annotation { "Feature Type Name" : "Feature", "Feature Type Description" : "" }
export const myFeature = defineFeature(function(context is Context, id is Id, definition is map)
    precondition{}
    {
        {
            var Q0;
            Q0=qCreatedBy(makeId("Top.planeOp"),FACE);
            var sketch = newSketch(context, id + "F0", { "sketchPlane" : qUnion([Q0])});
            skLineSegment(sketch, "E0.bottom", {"start": v(-839.09, -403.11) * mm, "end": v(831.05, -403.11) * mm});
            skLineSegment(sketch, "E0.left", {"start": v(-839.09, -403.11) * mm, "end": v(-839.09, -466.48) * mm});
            skLineSegment(sketch, "E0.right", {"start": v(831.05, -403.11) * mm, "end": v(831.05, -466.48) * mm});
            skLineSegment(sketch, "E1.bottom", {"start": v(761.55, -403.11) * mm, "end": v(831.05, -403.11) * mm});
            skLineSegment(sketch, "E1.top", {"start": v(761.55, 445.24) * mm, "end": v(831.05, 445.24) * mm});
            skLineSegment(sketch, "E1.left", {"start": v(761.55, -403.11) * mm, "end": v(761.55, 445.24) * mm});
            skLineSegment(sketch, "E1.right", {"start": v(831.05, -403.11) * mm, "end": v(831.05, 445.24) * mm});
            skLineSegment(sketch, "E2.bottom", {"start": v(761.55, 445.24) * mm, "end": v(-792.07, 445.24) * mm});
            skLineSegment(sketch, "E2.top", {"start": v(761.55, 390.05) * mm, "end": v(-792.07, 390.05) * mm});
            skLineSegment(sketch, "E2.left", {"start": v(761.55, 445.24) * mm, "end": v(761.55, 390.05) * mm});
            skLineSegment(sketch, "E2.right", {"start": v(-792.07, 445.24) * mm, "end": v(-792.07, 390.05) * mm});
            skLineSegment(sketch, "E3", {"start": v(-839.09, -466.48) * mm, "end": v(831.05, -466.48) * mm});
            skLineSegment(sketch, "E4.bottom", {"start": v(-792.07, 445.24) * mm, "end": v(-839.09, 445.24) * mm});
            skLineSegment(sketch, "E4.top", {"start": v(-792.07, -403.11) * mm, "end": v(-839.09, -403.11) * mm});
            skLineSegment(sketch, "E4.left", {"start": v(-792.07, 445.24) * mm, "end": v(-792.07, -403.11) * mm});
            skLineSegment(sketch, "E4.right", {"start": v(-839.09, 445.24) * mm, "end": v(-839.09, -403.11) * mm});
            skSolve(sketch);
        }
        {
            var Q0;
            Q0=makeQuery(id+"F0.imprint","IMPRINT",FACE,{"disambiguationData":[TD([[makeQuery(id+"F0.imprint","IMPRINT",EDGE,{"derivedFrom":sQuery(id+"F0.wireOp",EDGE,"E2.right")}),-1.0]])]});
            var Q1;
            {var subQ0=sQuery(id+"F0.wireOp",EDGE,"E0.left");Q1=makeQuery(id+"F0.imprint","IMPRINT",FACE,{"disambiguationData":[TD([[makeQuery(id+"F0.imprint","IMPRINT",EDGE,{"derivedFrom":subQ0}),1.0]])]});}
            var Q2;
            {var subQ0=sQuery(id+"F0.wireOp",EDGE,"E2.bottom");Q2=makeQuery(id+"F0.imprint","IMPRINT",FACE,{"disambiguationData":[TD([[makeQuery(id+"F0.imprint","IMPRINT",EDGE,{"derivedFrom":subQ0}),1.0]])]});}
            var Q3;
            {var subQ1=sQuery(id+"F0.wireOp",EDGE,"E1.top");Q3=makeQuery(id+"F0.imprint","IMPRINT",FACE,{"disambiguationData":[TD([[makeQuery(id+"F0.imprint","IMPRINT",EDGE,{"derivedFrom":subQ1}),-1.0]])]});}
            extrude(context, id + "F1", {"entities" : qUnion([Q0, Q1, Q2, Q3]), "depth" : 50.8 * mm, "offsetDistance" : 25.4 * mm});
        }
        {
            var Q0;
            Q0=makeQuery(id+"F1.opExtrude","SWEPT_FACE",FACE,{"disambiguationData":[OSD([sQuery(id+"F0.wireOp",EDGE,"E4.left")])]});
            extrude(context, id + "F2", {"entities" : qUnion([Q0]), "operationType" : NewBodyOperationType.ADD, "depth" : 1554.48 * mm, "offsetDistance" : 25.4 * mm});
        }
        {
            var Q0;
            {var subQ0=sQuery(id+"F0.wireOp",EDGE,"E4.left");Q0=makeQuery(id+"F2.boolean.opBoolean","MERGE",FACE,{"derivedFrom":[makeQuery(id+"F1.opExtrude","CAP_FACE",FACE,{"disambiguationData":[OSD([sQuery(id+"F0.wireOp",EDGE,"E0.bottom"),sQuery(id+"F0.wireOp",EDGE,"E0.left"),sQuery(id+"F0.wireOp",EDGE,"E0.right"),sQuery(id+"F0.wireOp",EDGE,"E1.top"),sQuery(id+"F0.wireOp",EDGE,"E1.left"),sQuery(id+"F0.wireOp",EDGE,"E1.right"),sQuery(id+"F0.wireOp",EDGE,"E2.bottom"),sQuery(id+"F0.wireOp",EDGE,"E2.top"),sQuery(id+"F0.wireOp",EDGE,"E3"),sQuery(id+"F0.wireOp",EDGE,"E4.bottom"),subQ0,sQuery(id+"F0.wireOp",EDGE,"E4.right")])],"isStart":false}),makeQuery(id+"F2.opExtrude","SWEPT_FACE",FACE,{"disambiguationData":[OSD([subQ0]),TDD([makeQuery(id+"F1.opExtrude","CAP_EDGE",EDGE,{"disambiguationData":[OSD([subQ0])],"isStart":false})])]})]});}
            var sketch = newSketch(context, id + "F3", { "sketchPlane" : qUnion([Q0])});
            skCircle(sketch, "E5.cCircle", {"center": v(-656.91, 28.1) * mm, "radius": 162.8 * mm, "construction": true});
            skLineSegment(sketch, "E5.0", {"start": v(-494.1, 122.1) * mm, "end": v(-494.1, -65.9) * mm});
            skLineSegment(sketch, "E5.1", {"start": v(-494.1, -65.9) * mm, "end": v(-656.91, -159.89) * mm});
            skLineSegment(sketch, "E5.2", {"start": v(-656.91, -159.89) * mm, "end": v(-819.72, -65.9) * mm});
            skLineSegment(sketch, "E5.3", {"start": v(-819.72, -65.9) * mm, "end": v(-819.72, 122.1) * mm});
            skLineSegment(sketch, "E5.4", {"start": v(-819.72, 122.1) * mm, "end": v(-656.91, 216.1) * mm});
            skLineSegment(sketch, "E5.5", {"start": v(-656.91, 216.1) * mm, "end": v(-494.1, 122.1) * mm});
            skPoint(sketch, "E5.0.midPoint", {"position": v(-494.1, 28.1) * mm});
            skFitSpline(sketch, "E6", {"points": [v(-229.05, 223.86) * mm, v(-44.25, 99.2) * mm, v(29.96, 322.2) * mm, v(-229.05, 223.86) * mm]});
            skText(sketch, "E7", { "text": "Asa Nichols", "fontName": "OpenSans-Regular.ttf"});
            const initialGuessF3  = {"E7": [-0.78519, -0.40369, 1, 0, 0.21011]};
            skSetInitialGuess(sketch, initialGuessF3);
            skSolve(sketch);
        }
        {
            var Q0;
            Q0 = qSketchRegion(id + "F3", true);
            var Q1;
            Q1 = qSketchRegion(id + "F5", true);
            extrude(context, id + "F4", {"entities" : qUnion([Q0, Q1]), "operationType" : NewBodyOperationType.ADD, "depth" : 25.4 * mm, "offsetDistance" : 25.4 * mm, "hasDraft" : true, "draftAngle" : 20 * degree});
        }
        {
            var Q0;
            Q0=makeQuery(id+"F3.imprint","IMPRINT",FACE,{"disambiguationData":[TD([[makeQuery(id+"F3.imprint","IMPRINT",EDGE,{"derivedFrom":sQuery(id+"F3.wireOp",EDGE,"E5.0")}),1.0]])]});
            var sketch = newSketch(context, id + "F5", { "sketchPlane" : qUnion([Q0])});
            skCircle(sketch, "E8", {"center": v(577.4, 265.35) * mm, "radius": 135.54 * mm});
            skSolve(sketch);
        }
        {
            var Q0;
            Q0=makeQuery(id+"F5.imprint","IMPRINT",FACE,{"disambiguationData":[TD([[makeQuery(id+"F5.imprint","IMPRINT",EDGE,{"derivedFrom":sQuery(id+"F5.wireOp",EDGE,"E8")}),1.0]])]});
            extrude(context, id + "F6", {"entities" : qUnion([Q0]), "operationType" : NewBodyOperationType.REMOVE, "oppositeDirection" : true, "depth" : 76.2 * mm, "offsetDistance" : 25.4 * mm});
        }
    });